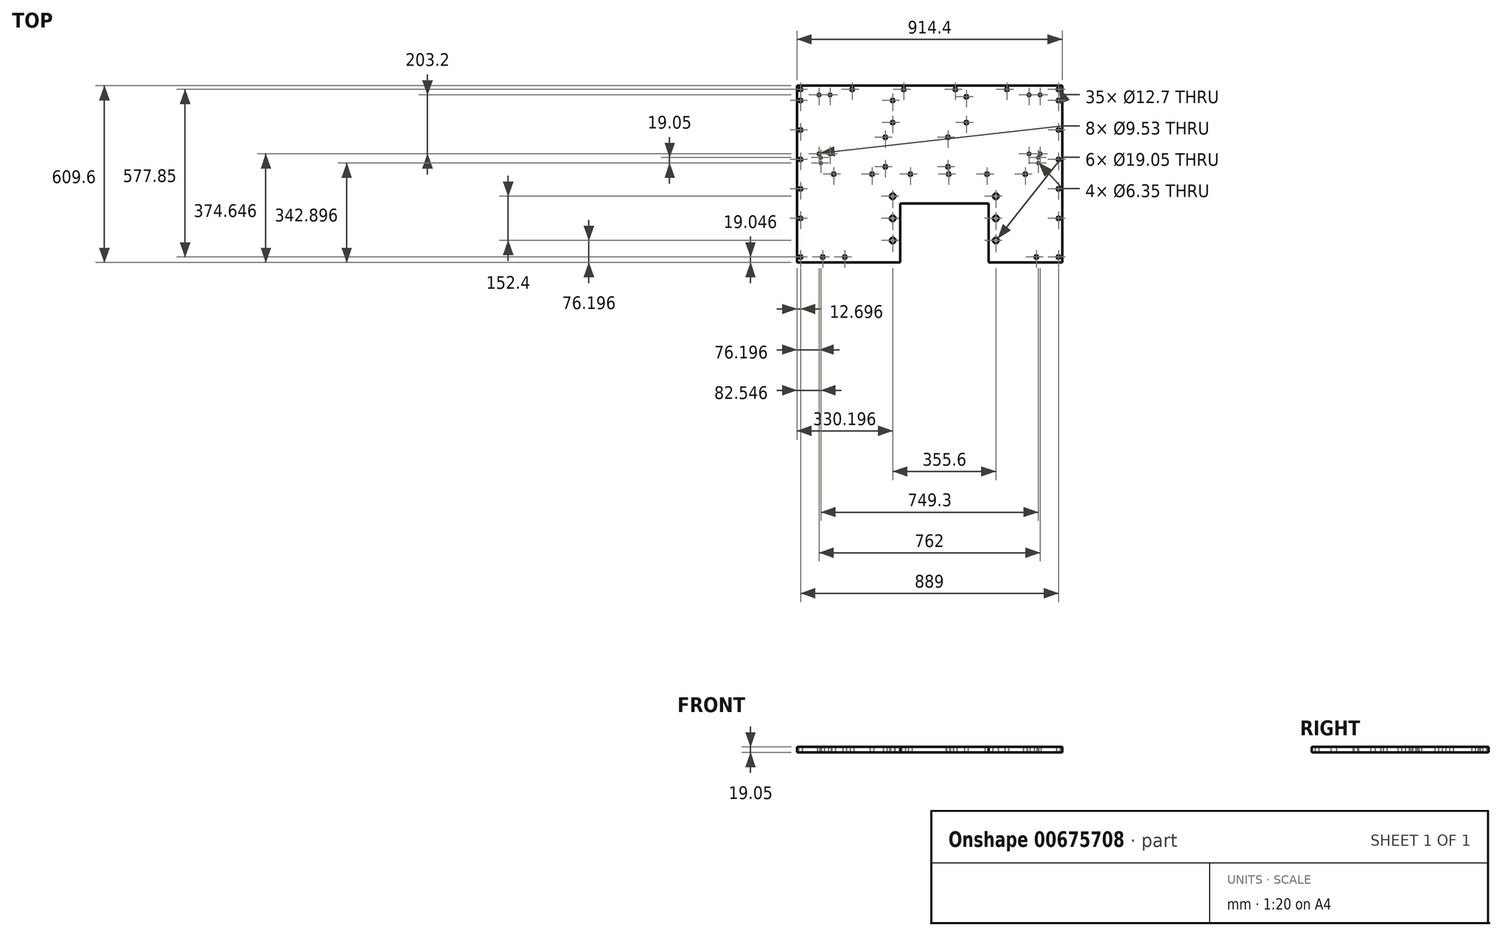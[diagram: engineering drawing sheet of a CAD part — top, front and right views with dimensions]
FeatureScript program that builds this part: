
annotation { "Feature Type Name" : "Feature", "Feature Type Description" : "" }
export const myFeature = defineFeature(function(context is Context, id is Id, definition is map)
    precondition{}
    {
        {
            var Q0;
            Q0=qCreatedBy(makeId("Top.planeOp"),FACE);
            var sketch = newSketch(context, id + "F0", { "sketchPlane" : qUnion([Q0])});
            skLineSegment(sketch, "E0", {"start": v(-479.58, 321.85) * mm, "end": v(-479.58, -287.75) * mm});
            skLineSegment(sketch, "E1", {"start": v(-479.58, -287.75) * mm, "end": v(-123.98, -287.75) * mm});
            skLineSegment(sketch, "E2", {"start": v(-123.98, -287.75) * mm, "end": v(-123.98, -84.55) * mm});
            skLineSegment(sketch, "E3", {"start": v(-123.98, -84.55) * mm, "end": v(180.82, -84.55) * mm});
            skLineSegment(sketch, "E4", {"start": v(180.82, -84.55) * mm, "end": v(180.82, -287.75) * mm});
            skLineSegment(sketch, "E5", {"start": v(180.82, -287.75) * mm, "end": v(434.82, -287.75) * mm});
            skLineSegment(sketch, "E6", {"start": v(434.82, -287.75) * mm, "end": v(434.82, 321.85) * mm});
            skLineSegment(sketch, "E7", {"start": v(434.82, 321.85) * mm, "end": v(-479.58, 321.85) * mm});
            skSolve(sketch);
        }
        {
            var Q0;
            Q0=makeQuery(id+"F0.imprint","IMPRINT",FACE,{"disambiguationData":[TD([[makeQuery(id+"F0.imprint","IMPRINT",EDGE,{"derivedFrom":sQuery(id+"F0.wireOp",EDGE,"E0")}),1.0]])]});
            extrude(context, id + "F1", {"entities" : qUnion([Q0]), "depth" : 19.05 * mm, "offsetDistance" : 25.4 * mm});
        }
        {
            var Q0;
            Q0=makeQuery(id+"F1.opExtrude","CAP_FACE",FACE,{"disambiguationData":[OSD([sQuery(id+"F0.wireOp",EDGE,"E0"),sQuery(id+"F0.wireOp",EDGE,"E1"),sQuery(id+"F0.wireOp",EDGE,"E2"),sQuery(id+"F0.wireOp",EDGE,"E3"),sQuery(id+"F0.wireOp",EDGE,"E4"),sQuery(id+"F0.wireOp",EDGE,"E5"),sQuery(id+"F0.wireOp",EDGE,"E6"),sQuery(id+"F0.wireOp",EDGE,"E7")])],"isStart":false});
            var sketch = newSketch(context, id + "F2", { "sketchPlane" : qUnion([Q0])});
            skCircle(sketch, "E8", {"center": v(-149.38, -135.35) * mm, "radius": 9.53 * mm});
            skCircle(sketch, "E9", {"center": v(-149.38, -59.15) * mm, "radius": 9.53 * mm});
            skCircle(sketch, "E10", {"center": v(-149.38, -211.55) * mm, "radius": 9.53 * mm});
            skCircle(sketch, "E11", {"center": v(206.22, -59.15) * mm, "radius": 9.53 * mm});
            skCircle(sketch, "E12", {"center": v(206.22, -135.35) * mm, "radius": 9.53 * mm});
            skCircle(sketch, "E13", {"center": v(206.22, -211.55) * mm, "radius": 9.53 * mm});
            skSolve(sketch);
        }
        {
            var Q0;
            Q0=makeQuery(id+"F2.imprint","IMPRINT",FACE,{"disambiguationData":[TD([[makeQuery(id+"F2.imprint","IMPRINT",EDGE,{"derivedFrom":sQuery(id+"F2.wireOp",EDGE,"E9")}),1.0]])]});
            var Q1;
            Q1=makeQuery(id+"F2.imprint","IMPRINT",FACE,{"disambiguationData":[TD([[makeQuery(id+"F2.imprint","IMPRINT",EDGE,{"derivedFrom":sQuery(id+"F2.wireOp",EDGE,"E8")}),1.0]])]});
            var Q2;
            Q2=makeQuery(id+"F2.imprint","IMPRINT",FACE,{"disambiguationData":[TD([[makeQuery(id+"F2.imprint","IMPRINT",EDGE,{"derivedFrom":sQuery(id+"F2.wireOp",EDGE,"E10")}),1.0]])]});
            var Q3;
            Q3=makeQuery(id+"F2.imprint","IMPRINT",FACE,{"disambiguationData":[TD([[makeQuery(id+"F2.imprint","IMPRINT",EDGE,{"derivedFrom":sQuery(id+"F2.wireOp",EDGE,"E13")}),1.0]])]});
            var Q4;
            Q4=makeQuery(id+"F2.imprint","IMPRINT",FACE,{"disambiguationData":[TD([[makeQuery(id+"F2.imprint","IMPRINT",EDGE,{"derivedFrom":sQuery(id+"F2.wireOp",EDGE,"E12")}),1.0]])]});
            var Q5;
            Q5=makeQuery(id+"F2.imprint","IMPRINT",FACE,{"disambiguationData":[TD([[makeQuery(id+"F2.imprint","IMPRINT",EDGE,{"derivedFrom":sQuery(id+"F2.wireOp",EDGE,"E11")}),1.0]])]});
            extrude(context, id + "F3", {"entities" : qUnion([Q0, Q1, Q2, Q3, Q4, Q5]), "operationType" : NewBodyOperationType.REMOVE, "oppositeDirection" : true, "depth" : 19.05 * mm, "offsetDistance" : 25.4 * mm});
        }
        {
            var Q0;
            Q0=makeQuery(id+"F1.opExtrude","CAP_FACE",FACE,{"disambiguationData":[OSD([sQuery(id+"F0.wireOp",EDGE,"E0"),sQuery(id+"F0.wireOp",EDGE,"E1"),sQuery(id+"F0.wireOp",EDGE,"E2"),sQuery(id+"F0.wireOp",EDGE,"E3"),sQuery(id+"F0.wireOp",EDGE,"E4"),sQuery(id+"F0.wireOp",EDGE,"E5"),sQuery(id+"F0.wireOp",EDGE,"E6"),sQuery(id+"F0.wireOp",EDGE,"E7")])],"isStart":false});
            var sketch = newSketch(context, id + "F4", { "sketchPlane" : qUnion([Q0])});
            skCircle(sketch, "E14", {"center": v(-466.88, -268.7) * mm, "radius": 6.35 * mm});
            skCircle(sketch, "E15", {"center": v(-390.68, -268.7) * mm, "radius": 6.35 * mm});
            skCircle(sketch, "E16", {"center": v(-314.48, -268.7) * mm, "radius": 6.35 * mm});
            skCircle(sketch, "E17", {"center": v(345.92, -268.7) * mm, "radius": 6.35 * mm});
            skCircle(sketch, "E18", {"center": v(422.12, -268.7) * mm, "radius": 6.35 * mm});
            skSolve(sketch);
        }
        {
            var Q0;
            Q0=makeQuery(id+"F4.imprint","IMPRINT",FACE,{"disambiguationData":[TD([[makeQuery(id+"F4.imprint","IMPRINT",EDGE,{"derivedFrom":sQuery(id+"F4.wireOp",EDGE,"E17")}),1.0]])]});
            var Q1;
            Q1=makeQuery(id+"F4.imprint","IMPRINT",FACE,{"disambiguationData":[TD([[makeQuery(id+"F4.imprint","IMPRINT",EDGE,{"derivedFrom":sQuery(id+"F4.wireOp",EDGE,"E18")}),1.0]])]});
            var Q2;
            Q2=makeQuery(id+"F4.imprint","IMPRINT",FACE,{"disambiguationData":[TD([[makeQuery(id+"F4.imprint","IMPRINT",EDGE,{"derivedFrom":sQuery(id+"F4.wireOp",EDGE,"E16")}),1.0]])]});
            var Q3;
            Q3=makeQuery(id+"F4.imprint","IMPRINT",FACE,{"disambiguationData":[TD([[makeQuery(id+"F4.imprint","IMPRINT",EDGE,{"derivedFrom":sQuery(id+"F4.wireOp",EDGE,"E15")}),1.0]])]});
            var Q4;
            Q4=makeQuery(id+"F4.imprint","IMPRINT",FACE,{"disambiguationData":[TD([[makeQuery(id+"F4.imprint","IMPRINT",EDGE,{"derivedFrom":sQuery(id+"F4.wireOp",EDGE,"E14")}),1.0]])]});
            extrude(context, id + "F5", {"entities" : qUnion([Q0, Q1, Q2, Q3, Q4]), "operationType" : NewBodyOperationType.REMOVE, "oppositeDirection" : true, "depth" : 19.05 * mm, "offsetDistance" : 25.4 * mm});
        }
        {
            var Q0;
            Q0=makeQuery(id+"F1.opExtrude","CAP_FACE",FACE,{"disambiguationData":[OSD([sQuery(id+"F0.wireOp",EDGE,"E0"),sQuery(id+"F0.wireOp",EDGE,"E1"),sQuery(id+"F0.wireOp",EDGE,"E2"),sQuery(id+"F0.wireOp",EDGE,"E3"),sQuery(id+"F0.wireOp",EDGE,"E4"),sQuery(id+"F0.wireOp",EDGE,"E5"),sQuery(id+"F0.wireOp",EDGE,"E6"),sQuery(id+"F0.wireOp",EDGE,"E7")])],"isStart":false});
            var sketch = newSketch(context, id + "F6", { "sketchPlane" : qUnion([Q0])});
            skCircle(sketch, "E19", {"center": v(-466.88, -135.35) * mm, "radius": 6.35 * mm});
            skCircle(sketch, "E20", {"center": v(-466.88, -33.75) * mm, "radius": 6.35 * mm});
            skCircle(sketch, "E21", {"center": v(-466.88, 169.45) * mm, "radius": 6.35 * mm});
            skCircle(sketch, "E22", {"center": v(-466.88, 67.85) * mm, "radius": 6.35 * mm});
            skCircle(sketch, "E23", {"center": v(422.12, -33.75) * mm, "radius": 6.35 * mm});
            skCircle(sketch, "E24", {"center": v(422.12, 67.85) * mm, "radius": 6.35 * mm});
            skCircle(sketch, "E25", {"center": v(422.12, 169.45) * mm, "radius": 6.35 * mm});
            skCircle(sketch, "E26", {"center": v(422.12, 271.05) * mm, "radius": 6.35 * mm});
            skCircle(sketch, "E27", {"center": v(422.12, -135.35) * mm, "radius": 6.35 * mm});
            skCircle(sketch, "E28", {"center": v(-466.88, 271.05) * mm, "radius": 6.35 * mm});
            skCircle(sketch, "E29", {"center": v(-466.88, 309.15) * mm, "radius": 6.35 * mm});
            skCircle(sketch, "E30", {"center": v(422.12, 309.15) * mm, "radius": 6.35 * mm});
            skCircle(sketch, "E31", {"center": v(-289.08, 309.15) * mm, "radius": 6.35 * mm});
            skCircle(sketch, "E32", {"center": v(-111.28, 309.15) * mm, "radius": 6.35 * mm});
            skCircle(sketch, "E33", {"center": v(66.52, 309.15) * mm, "radius": 6.35 * mm});
            skCircle(sketch, "E34", {"center": v(244.32, 309.15) * mm, "radius": 6.35 * mm});
            skCircle(sketch, "E35", {"center": v(-149.38, 271.05) * mm, "radius": 6.35 * mm});
            skCircle(sketch, "E36", {"center": v(104.62, 283.75) * mm, "radius": 6.35 * mm});
            skCircle(sketch, "E37", {"center": v(-149.38, 194.85) * mm, "radius": 6.35 * mm});
            skCircle(sketch, "E38", {"center": v(104.62, 194.85) * mm, "radius": 6.35 * mm});
            skCircle(sketch, "E39", {"center": v(-352.58, 17.05) * mm, "radius": 6.35 * mm});
            skPoint(sketch, "E39.centerSnap0", {"position": v(-479.58, 17.05) * mm});
            skCircle(sketch, "E40", {"center": v(-220.5, 17.05) * mm, "radius": 6.35 * mm});
            skCircle(sketch, "E41", {"center": v(-88.42, 17.05) * mm, "radius": 6.35 * mm});
            skCircle(sketch, "E42", {"center": v(43.66, 17.05) * mm, "radius": 6.35 * mm});
            skCircle(sketch, "E43", {"center": v(175.74, 17.05) * mm, "radius": 6.35 * mm});
            skCircle(sketch, "E44", {"center": v(307.82, 17.05) * mm, "radius": 6.35 * mm});
            skCircle(sketch, "E45", {"center": v(-174.78, 144.05) * mm, "radius": 6.35 * mm});
            skCircle(sketch, "E46", {"center": v(41.12, 144.05) * mm, "radius": 6.35 * mm});
            skCircle(sketch, "E47", {"center": v(-174.78, 42.45) * mm, "radius": 6.35 * mm});
            skCircle(sketch, "E48", {"center": v(41.12, 42.45) * mm, "radius": 6.35 * mm});
            skSolve(sketch);
        }
        {
            var Q0;
            Q0 = qSketchRegion(id + "F6", true);
            extrude(context, id + "F7", {"entities" : qUnion([Q0]), "operationType" : NewBodyOperationType.REMOVE, "oppositeDirection" : true, "depth" : 19.05 * mm, "offsetDistance" : 25.4 * mm});
        }
        {
            var Q0;
            Q0 = qSketchRegion(id + "F4", true);
            extrude(context, id + "F8", {"entities" : qUnion([Q0]), "operationType" : NewBodyOperationType.REMOVE, "oppositeDirection" : true, "depth" : 19.05 * mm, "offsetDistance" : 25.4 * mm});
        }
        {
            var Q0;
            Q0=makeQuery(id+"F1.opExtrude","CAP_FACE",FACE,{"disambiguationData":[OSD([sQuery(id+"F0.wireOp",EDGE,"E0"),sQuery(id+"F0.wireOp",EDGE,"E1"),sQuery(id+"F0.wireOp",EDGE,"E2"),sQuery(id+"F0.wireOp",EDGE,"E3"),sQuery(id+"F0.wireOp",EDGE,"E4"),sQuery(id+"F0.wireOp",EDGE,"E5"),sQuery(id+"F0.wireOp",EDGE,"E6"),sQuery(id+"F0.wireOp",EDGE,"E7")])],"isStart":false});
            var sketch = newSketch(context, id + "F9", { "sketchPlane" : qUnion([Q0])});
            skCircle(sketch, "E49", {"center": v(-403.38, 290.1) * mm, "radius": 4.76 * mm});
            skCircle(sketch, "E50", {"center": v(-365.28, 290.1) * mm, "radius": 4.76 * mm});
            skCircle(sketch, "E51", {"center": v(320.52, 290.1) * mm, "radius": 4.76 * mm});
            skCircle(sketch, "E52", {"center": v(358.62, 290.1) * mm, "radius": 4.76 * mm});
            skCircle(sketch, "E53", {"center": v(-403.38, 86.9) * mm, "radius": 4.76 * mm});
            skCircle(sketch, "E54", {"center": v(-365.28, 86.9) * mm, "radius": 4.76 * mm});
            skCircle(sketch, "E55", {"center": v(320.52, 86.9) * mm, "radius": 4.76 * mm});
            skCircle(sketch, "E56", {"center": v(358.62, 86.9) * mm, "radius": 4.76 * mm});
            skSolve(sketch);
        }
        {
            var Q0;
            Q0 = qSketchRegion(id + "F9", true);
            extrude(context, id + "F10", {"entities" : qUnion([Q0]), "operationType" : NewBodyOperationType.REMOVE, "oppositeDirection" : true, "depth" : 19.05 * mm, "offsetDistance" : 25.4 * mm});
        }
        {
            var Q0;
            Q0=makeQuery(id+"F1.opExtrude","CAP_FACE",FACE,{"disambiguationData":[OSD([sQuery(id+"F0.wireOp",EDGE,"E0"),sQuery(id+"F0.wireOp",EDGE,"E1"),sQuery(id+"F0.wireOp",EDGE,"E2"),sQuery(id+"F0.wireOp",EDGE,"E3"),sQuery(id+"F0.wireOp",EDGE,"E4"),sQuery(id+"F0.wireOp",EDGE,"E5"),sQuery(id+"F0.wireOp",EDGE,"E6"),sQuery(id+"F0.wireOp",EDGE,"E7")])],"isStart":false});
            var sketch = newSketch(context, id + "F11", { "sketchPlane" : qUnion([Q0])});
            skCircle(sketch, "E57", {"center": v(-397.03, 74.2) * mm, "radius": 3.18 * mm});
            skCircle(sketch, "E58", {"center": v(-397.03, 55.15) * mm, "radius": 3.18 * mm});
            skCircle(sketch, "E59", {"center": v(352.27, 74.2) * mm, "radius": 3.18 * mm});
            skCircle(sketch, "E60", {"center": v(352.27, 55.15) * mm, "radius": 3.18 * mm});
            skSolve(sketch);
        }
        {
            var Q0;
            Q0 = qSketchRegion(id + "F11", true);
            extrude(context, id + "F12", {"entities" : qUnion([Q0]), "operationType" : NewBodyOperationType.REMOVE, "oppositeDirection" : true, "depth" : 19.05 * mm, "offsetDistance" : 25.4 * mm});
        }
    });
